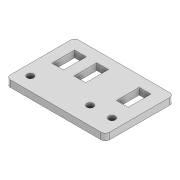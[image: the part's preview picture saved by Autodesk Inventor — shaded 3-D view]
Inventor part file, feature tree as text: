
AUTODESK INVENTOR PART (.ipt)
format: ipt  version: 2022 (Build 260153000, 153)  size: 150,528 bytes
history: native  units: mm
features: thicken_offset x3, extrude x1, fillet x1
ambient origin geometry x8: Origin, YZ Plane, XZ Plane, XY Plane, X Axis, Y Axis, Z Axis, Center Point
bodies: Solid1 (feature_tree)
feature tree (5):
  extrude  "Extrusion1"  Depth=3.0mm
  fillet  "Fillet1"  Radius=3.0mm
  thicken_offset  "Thicken1"
  thicken_offset  "Thicken2"
  thicken_offset  "Thicken3"
